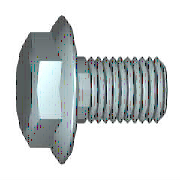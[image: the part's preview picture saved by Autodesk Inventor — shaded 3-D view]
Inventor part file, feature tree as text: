
AUTODESK INVENTOR PART (.ipt)
format: ipt  version: 2022 (Build 260153000, 153)  size: 201,216 bytes
history: native  units: mm (DEFAULTED — no unit token found)
features: sketch x3, extrude x1, chamfer x1, plane x1
ambient origin geometry x7: Origin, YZ Plane, XZ Plane, X Axis, Y Axis, Z Axis, Center Point
bodies: Solid1 (feature_tree), Body (feature_tree)
feature tree (6):
  extrude  "Head"  Depth=80.0mm
  chamfer  "Chamfer1"  Distance=8.0mm
  plane  "Work Plane1"
  sketch  "Sketch1"  dims[d0=1.2mm d1=80.0mm]
  sketch  "Sketch2"  dims[d2=22.0mm]
  sketch  "Sketch3"  dims[d3=17.0mm d4=8.0mm d5=3.825mm d12=90.0deg d6=8.5mm d7=0.0mm d8=30.0deg d21=90.0deg d10=22.0mm d11=0.0mm d13=0.766813mm d14=0.766813mm d15=8.0mm d16=8.0mm d17=0.0001mm d18=0.766813mm d19=4.363323mm d20=0.0mm d22=9.5mm d23=10.0mm d39=45.0deg d40=0.0mm d41=0.0mm]
